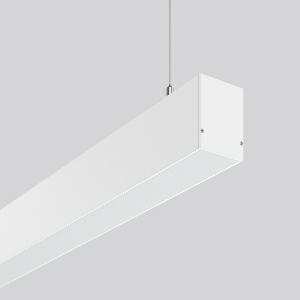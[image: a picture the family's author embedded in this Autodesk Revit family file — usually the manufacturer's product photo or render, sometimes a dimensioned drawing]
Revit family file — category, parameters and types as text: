
# Revit family: less_is_more_50_312318_002_1_85af
name_source: partatom
category: Lighting Fixtures
units: mm (PartAtom-declared; Revit-internal decimal feet)

## family parameters
Cut with Voids When Loaded = No
Host = Face
Light Source = No
Part Type = Normal
Room Calculation Point = No
Round Connector Dimension = Use Diameter
Shared = No

## types (1)
- LESS IS MORE 50 (1 x LED Modul 840, 4800 lm, 4000)
    Apparent Load = 40 VA
    CIE Flux Codes = 49 80 96 63 100
    Color Rendering = 80
    Color Temperature = 4000
    Default Elevation = 1800 mm
    Description = Series: LESS IS MORE 50
Linear pendant luminaire for aesthetically sophisticated lighting. Housing: extruded aluminium profile, powder-coated. End cap aluminium powder-coated. Canopy made of aluminium, powder-coated. Diffuser made of non-yellowing plastic (PMMA), opal. Direct 65%, indirect 35% light emission. Suitable for pendant. 2-point steel cable suspension freely positionable and infinitely height-adjustable. Special lengths available on request. LED unit with integrated converter interchangeable and removable. Suitable for through-wiring. With sensors or as a safety luminaire on request. 
Colour: traffic white, matt (RAL 9016)
Length: 1127 mm
Width: 57 mm
Height: 75 mm
Suspension length: 2000 mm
Lamp: LED
Socket: without socket
Colour temperature: 4000K
Colour rendering index (CRI): 80
Light source: LED
Socket lamp2: Without base
Colour temperature: 4000K
System power: 40 W
Rated luminous flux: 4800 lm
Luminous efficiency: 120 lm/W
Control gear: Regulated power supply
Control gear: Regulated power supply
Protection class: I
Type of protection: IP 20
    Height = 75 mm
    Lamp = 1 x LED Modul 840
    Lamp Light Flux = 4800 lm
    Lamp count = 1
    Length = 1127 mm
    Lifetime = 50000 h
    Luminous efficacy = 120 lm/W
    Manufacturer = RZB
    ModVariant = No
    Model = 312318.002.1
    Mounting Place = Ceiling
    Mounting Type = Pendant
    Number of Poles = 1
    OnlyDefault = Yes
    Power Factor = 1
    Product Name = LESS IS MORE 50
    Product group = Pendant LED linear luminaires
    ProductGroupID = 907
    Protection Class = Protection class I
    Protection Degree = IP 20
    RLX_Detail_Level = 1
    RLX_Emergency_Light_Flux = 0 lm
    RLX_Emergency_Type = 0
    RLX_Emergency_Type_DB = No
    RlxData = <blob elided: 31653 chars, md5=f3c644e6>
    Socket = socket
    Standby Power = 0 W
    System Light Flux = 4800 lm
    System Power = 40 W
    Type Comments = Product without accessories
    Type Image = 312318.002.jpg
    URL = http://relux.com
    VarID = ---
    Voltage = 230 V
    Voltage Range = 220-240 V
    Weight = 0.00 kg
    Width = 57 mm

## geometry (parser evidence)
native form markers: Blend x4, Sweep x13
no freeform markers — native parametric forms only
